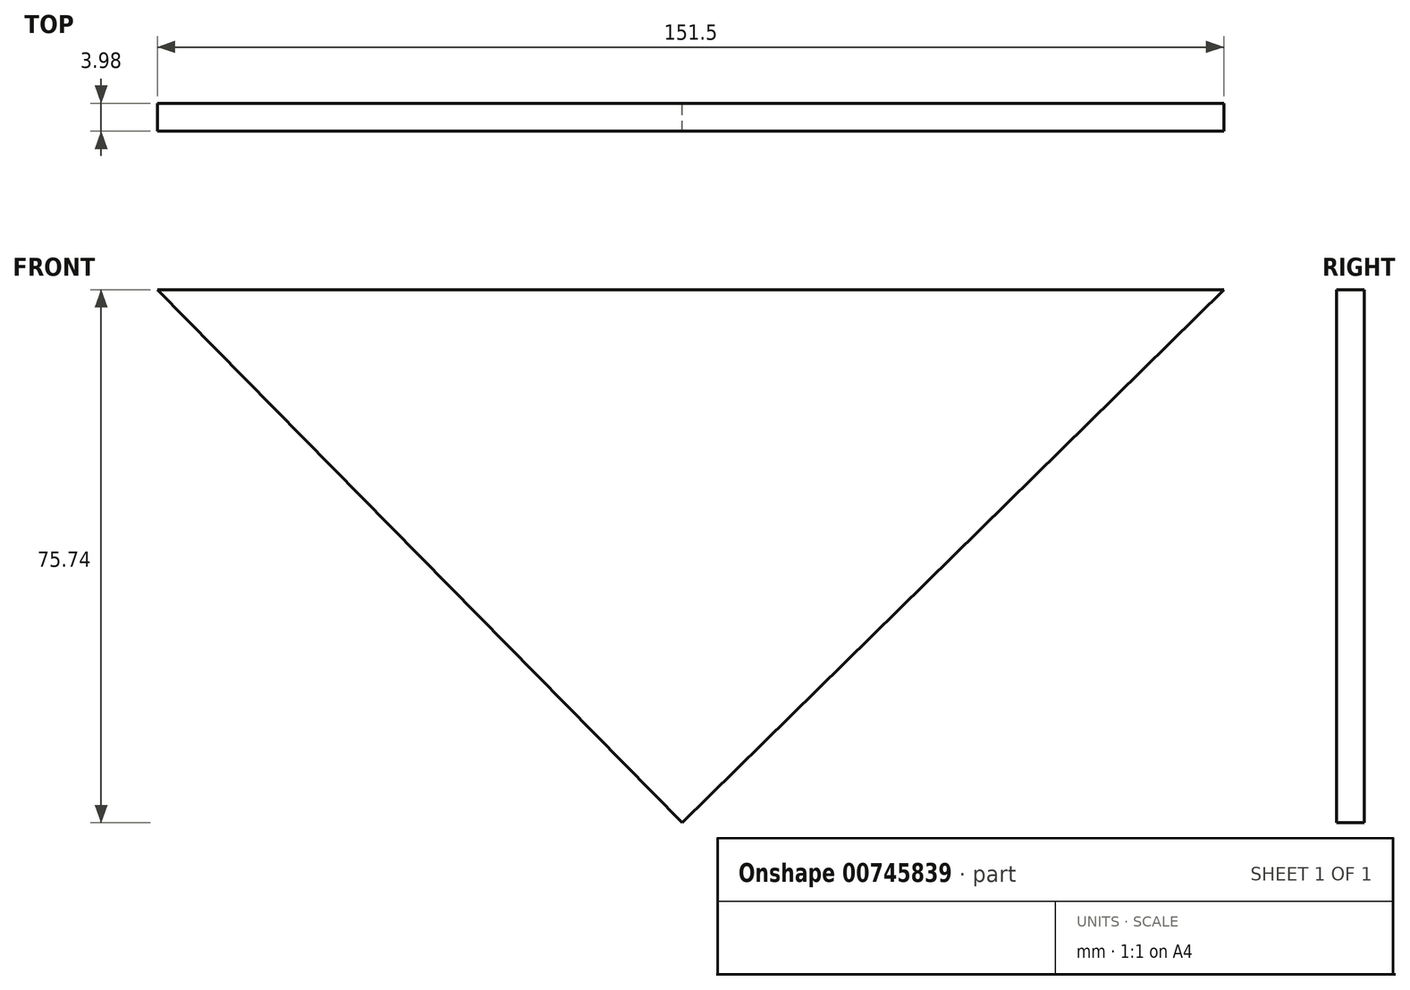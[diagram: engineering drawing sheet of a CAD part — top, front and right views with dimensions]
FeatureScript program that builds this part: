
annotation { "Feature Type Name" : "Feature", "Feature Type Description" : "" }
export const myFeature = defineFeature(function(context is Context, id is Id, definition is map)
    precondition{}
    {
        {
            var Q0;
            Q0=qCreatedBy(makeId("Front.planeOp"),FACE);
            var sketch = newSketch(context, id + "F0", { "sketchPlane" : qUnion([Q0])});
            skLineSegment(sketch, "E0", {"start": v(-74.56, 0) * mm, "end": v(0, -75.74) * mm});
            skLineSegment(sketch, "E1", {"start": v(0, -75.74) * mm, "end": v(76.94, 0) * mm});
            skLineSegment(sketch, "E2", {"start": v(76.94, 0) * mm, "end": v(-74.56, 0) * mm});
            skSolve(sketch);
        }
        {
            var Q0;
            Q0=makeQuery(id+"F0.imprint","IMPRINT",FACE,{"disambiguationData":[TD([[makeQuery(id+"F0.imprint","IMPRINT",EDGE,{"derivedFrom":sQuery(id+"F0.wireOp",EDGE,"E0")}),1.0]])]});
            extrude(context, id + "F1", {"entities" : qUnion([Q0]), "depth" : 3.98 * mm, "offsetDistance" : 25.4 * mm});
        }
    });
